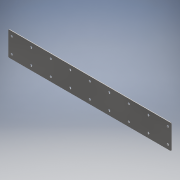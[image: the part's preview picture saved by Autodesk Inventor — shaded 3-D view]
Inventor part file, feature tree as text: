
AUTODESK INVENTOR PART (.ipt)
format: ipt  version: 2021 (Build 250183000, 183)  size: 137,216 bytes
history: native  units: mm
features: sketch x2, other x2, sheet_metal_op x1, pattern_linear x1, fillet x1
ambient origin geometry x8: Origin, YZ Plane, XZ Plane, XY Plane, X Axis, Y Axis, Z Axis, Center Point
bodies: Solid1 (feature_tree)
feature tree (7):
  sheet_metal_op  "Face1"
  pattern_linear  "Rectangular Pattern1"  Spacing1=3.0mm  [1 undecoded]
  fillet  "Fillet1"  Radius=10.7mm
  sketch  "Sketch1"  dims[d0=125.0mm]
  other  "Plate1"
  sketch  "Sketch2"  dims[d1=835.0mm d2=3.0mm d3=10.7mm d4=80.0mm d5=3.0mm d6=0.0mm d7=90.0mm d9=100.0mm d10=5.0mm]
  other  "Cut1"
note: 1 required parameter value undecoded (feature->parameter linkage not recoverable at this tier; creation-order binding heuristic only, values carry confidence <= 0.55)
